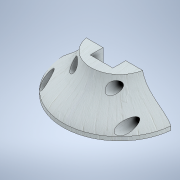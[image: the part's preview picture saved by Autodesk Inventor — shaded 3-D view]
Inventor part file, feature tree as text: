
AUTODESK INVENTOR PART (.ipt)
format: ipt  version: 2021 (Build 250183000, 183)  size: 280,576 bytes
history: native  units: mm
features: sketch x6, extrude x5, plane x2, revolve x1, split x1
ambient origin geometry x8: Origin, YZ Plane, XZ Plane, XY Plane, X Axis, Y Axis, Z Axis, Center Point
bodies: Solid1 (feature_tree)
feature tree (15):
  revolve  "Revolution1"  [1 undecoded]
  extrude  "Extrusion1"  Depth=5.0mm
  extrude  "Extrusion2"  Depth=30.0mm
  extrude  "Extrusion3"  Depth=24.0mm
  plane  "Work Plane1"
  split  "Split1"
  extrude  "Extrusion4"  Depth=35.0mm TaperAngle=0.0deg
  plane  "Work Plane2"
  extrude  "Extrusion5"  Depth=50.0mm TaperAngle=0.0deg
  sketch  "Sketch1"  dims[d0=75.0mm d1=50.0mm]
  sketch  "Sketch2"  dims[d2=38.0mm d3=5.0mm]
  sketch  "Sketch3"  dims[d4=90.0deg d5=30.0mm]
  sketch  "Sketch4"  dims[d6=48.0mm d7=24.0mm]
  sketch  "Sketch6"  dims[d8=15.0mm d9=35.0mm d10=0.0mm]
  sketch  "Sketch7"  dims[d11=17.0mm d12=8.0mm d13=0.0mm d14=5.2mm d15=5.2mm d16=12.0mm d17=12.0mm d18=22.0mm d19=12.0mm d20=52.0mm d21=52.0mm d22=0.0mm d23=0.0mm d24=0.0mm d25=21.0mm d26=2.5mm d27=0.0mm d28=-12.5mm d29=12.5mm d30=12.5mm d31=12.5mm d32=12.5mm d33=50.0mm d34=0.0mm]
note: 1 required parameter value undecoded (feature->parameter linkage not recoverable at this tier; creation-order binding heuristic only, values carry confidence <= 0.55)
